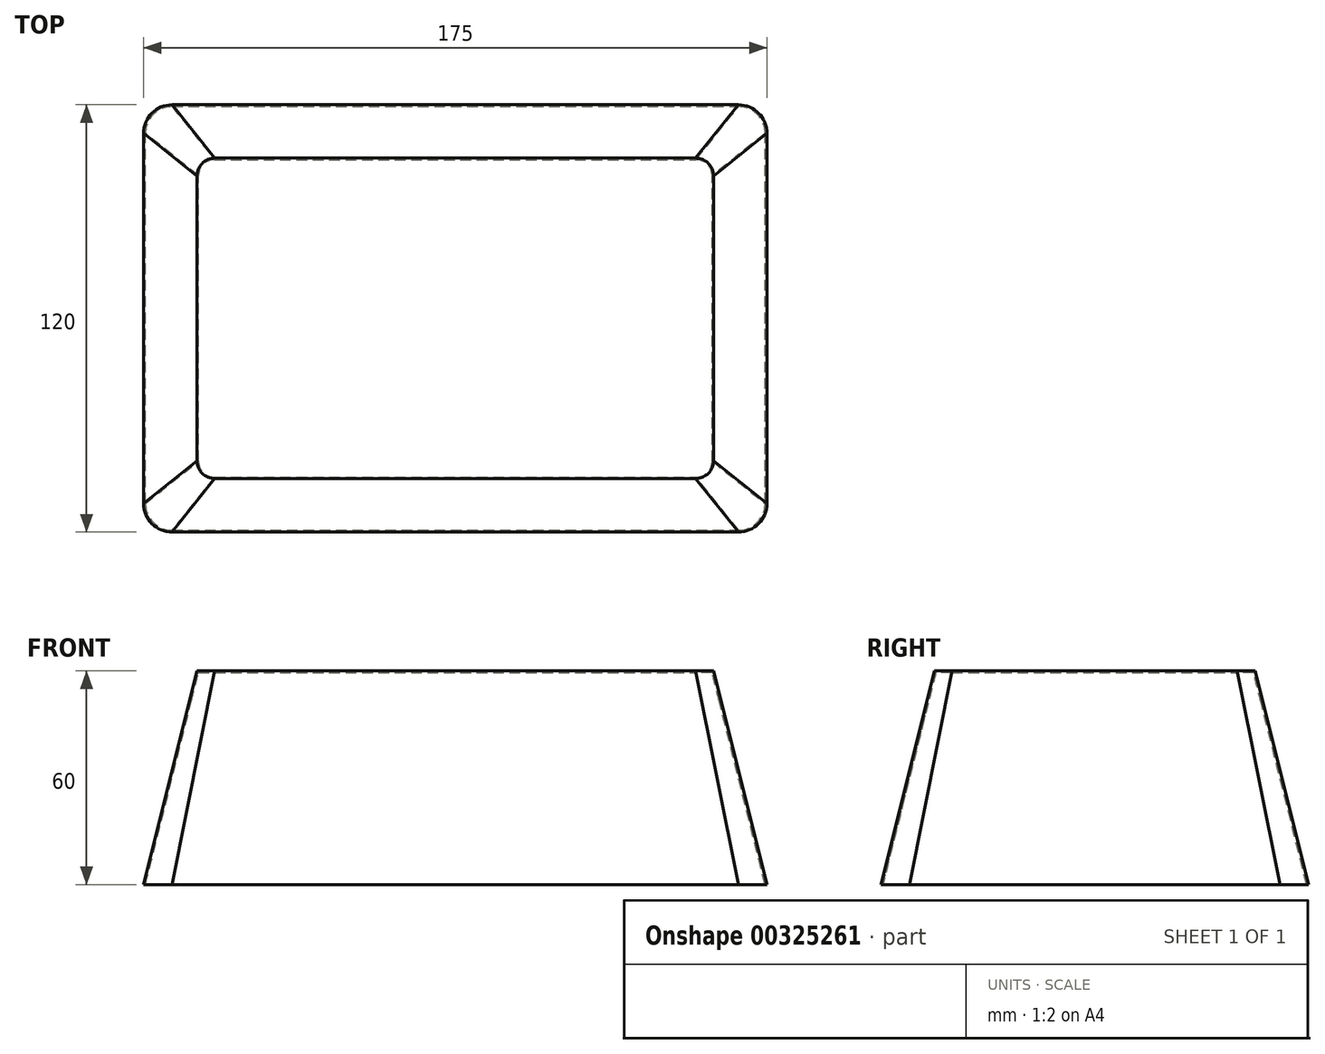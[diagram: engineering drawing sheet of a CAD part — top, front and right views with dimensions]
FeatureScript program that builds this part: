
annotation { "Feature Type Name" : "Feature", "Feature Type Description" : "" }
export const myFeature = defineFeature(function(context is Context, id is Id, definition is map)
    precondition{}
    {
        {
            var Q0;
            Q0=qCreatedBy(makeId("Top.planeOp"),FACE);
            var sketch = newSketch(context, id + "F0", { "sketchPlane" : qUnion([Q0])});
            skLineSegment(sketch, "E0.bottom", {"start": v(-79.5, -60) * mm, "end": v(79.5, -60) * mm});
            skLineSegment(sketch, "E0.top", {"start": v(-79.5, 60) * mm, "end": v(79.5, 60) * mm});
            skLineSegment(sketch, "E0.left", {"start": v(-87.5, -52) * mm, "end": v(-87.5, 52) * mm});
            skLineSegment(sketch, "E0.right", {"start": v(87.5, -52) * mm, "end": v(87.5, 52) * mm});
            skPoint(sketch, "E0.middle", {"position": v(0, 0) * mm});
            skPoint(sketch, "E1.visualSharp", {"position": v(-87.5, -60) * mm});
            skArc(sketch, "E1.filletArc", {"start": v(-87.5, -52) * mm, "mid": v(-85.16, -57.66) * mm, "end": v(-79.5, -60) * mm});
            skPoint(sketch, "E2.visualSharp", {"position": v(87.5, -60) * mm});
            skArc(sketch, "E2.filletArc", {"start": v(79.5, -60) * mm, "mid": v(85.16, -57.66) * mm, "end": v(87.5, -52) * mm});
            skPoint(sketch, "E3.visualSharp", {"position": v(87.5, 60) * mm});
            skArc(sketch, "E3.filletArc", {"start": v(87.5, 52) * mm, "mid": v(85.16, 57.66) * mm, "end": v(79.5, 60) * mm});
            skPoint(sketch, "E4.visualSharp", {"position": v(-87.5, 60) * mm});
            skArc(sketch, "E4.filletArc", {"start": v(-79.5, 60) * mm, "mid": v(-85.16, 57.66) * mm, "end": v(-87.5, 52) * mm});
            skSolve(sketch);
        }
        {
            var Q0;
            Q0=qCreatedBy(makeId("Top.planeOp"),FACE);
            cPlane(context, id + "F1", {"entities" : qUnion([Q0]), "cplaneType" : CPlaneType.OFFSET, "offset" : 60 * mm, "width" : 150 * mm, "height" : 150 * mm});
        }
        {
            var Q0;
            Q0=qCreatedBy(id+"F1.planeOp",FACE);
            var sketch = newSketch(context, id + "F2", { "sketchPlane" : qUnion([Q0])});
            skLineSegment(sketch, "E5.bottom", {"start": v(-67.5, 45) * mm, "end": v(67.5, 45) * mm});
            skLineSegment(sketch, "E5.top", {"start": v(-67.5, -45) * mm, "end": v(67.5, -45) * mm});
            skLineSegment(sketch, "E5.left", {"start": v(-72.5, 40) * mm, "end": v(-72.5, -40) * mm});
            skLineSegment(sketch, "E5.right", {"start": v(72.5, 40) * mm, "end": v(72.5, -40) * mm});
            skPoint(sketch, "E5.middle", {"position": v(0, 0) * mm});
            skPoint(sketch, "E6.visualSharp", {"position": v(-72.5, 45) * mm});
            skArc(sketch, "E6.filletArc", {"start": v(-67.5, 45) * mm, "mid": v(-71.04, 43.54) * mm, "end": v(-72.5, 40) * mm});
            skPoint(sketch, "E7.visualSharp", {"position": v(72.5, 45) * mm});
            skArc(sketch, "E7.filletArc", {"start": v(72.5, 40) * mm, "mid": v(71.04, 43.54) * mm, "end": v(67.5, 45) * mm});
            skPoint(sketch, "E8.visualSharp", {"position": v(72.5, -45) * mm});
            skArc(sketch, "E8.filletArc", {"start": v(67.5, -45) * mm, "mid": v(71.04, -43.54) * mm, "end": v(72.5, -40) * mm});
            skPoint(sketch, "E9.visualSharp", {"position": v(-72.5, -45) * mm});
            skArc(sketch, "E9.filletArc", {"start": v(-72.5, -40) * mm, "mid": v(-71.04, -43.54) * mm, "end": v(-67.5, -45) * mm});
            skSolve(sketch);
        }
        {
            var Q0;
            Q0 = qSketchRegion(id + "F0", true);
            var Q1;
            Q1 = qSketchRegion(id + "F2", true);
            loft(context, id + "F3", {"sheetProfilesArray" : [{ "sheetProfileEntities" : qUnion([Q0]) }, { "sheetProfileEntities" : qUnion([Q1]) }]});
        }
        {
            var Q0;
            Q0=makeQuery(id+"F3.opLoft","CAP_FACE",FACE,{"disambiguationData":[OSD([makeQuery(id+"F0.imprint","IMPRINT",FACE,{"disambiguationData":[TD([[makeQuery(id+"F0.imprint","IMPRINT",EDGE,{"derivedFrom":sQuery(id+"F0.wireOp",EDGE,"E0.bottom")}),1.0]])]})])],"isStart":true});
            shell(context, id + "F4", {"entities" : qUnion([Q0]), "thickness" : 0.5 * mm});
        }
    });
